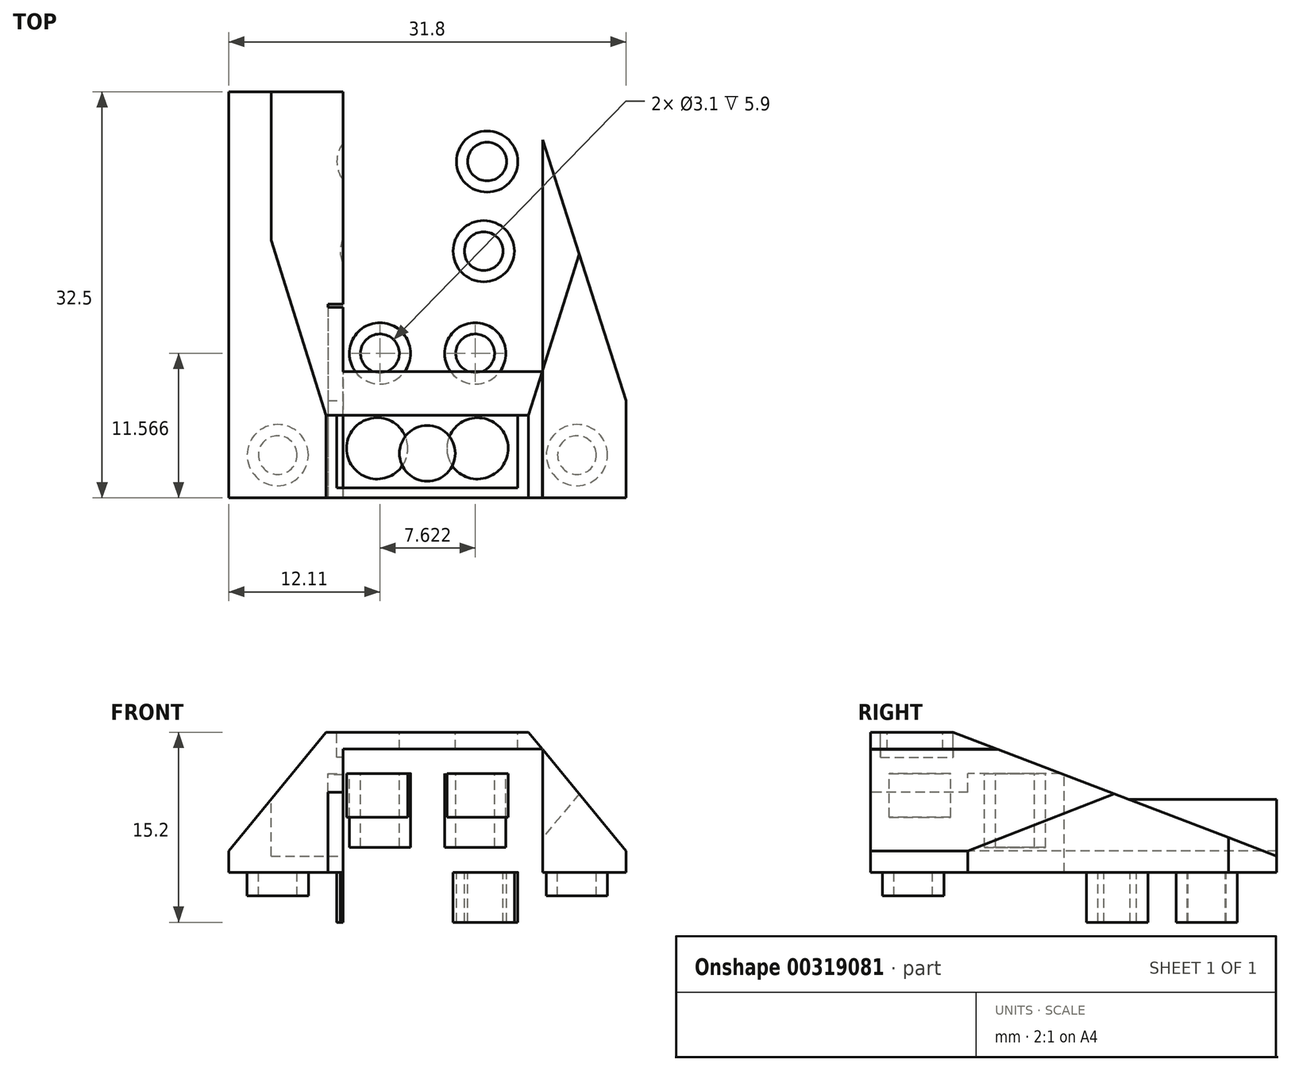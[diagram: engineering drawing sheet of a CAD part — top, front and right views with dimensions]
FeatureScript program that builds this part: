
annotation { "Feature Type Name" : "Feature", "Feature Type Description" : "" }
export const myFeature = defineFeature(function(context is Context, id is Id, definition is map)
    precondition{}
    {
        {
            var Q0;
            Q0=qCreatedBy(makeId("Front.planeOp"),FACE);
            var sketch = newSketch(context, id + "F0", { "sketchPlane" : qUnion([Q0])});
            skLineSegment(sketch, "E0.bottom", {"start": v(-15.9, 3.2) * mm, "end": v(15.9, 3.2) * mm});
            skLineSegment(sketch, "E0.top", {"start": v(-15.9, -6.5) * mm, "end": v(15.9, -6.5) * mm});
            skLineSegment(sketch, "E0.left", {"start": v(-15.9, 3.2) * mm, "end": v(-15.9, -6.5) * mm});
            skLineSegment(sketch, "E0.right", {"start": v(15.9, 3.2) * mm, "end": v(15.9, -6.5) * mm});
            skLineSegment(sketch, "E1.bottom", {"start": v(-6.73, -6.5) * mm, "end": v(9.23, -6.5) * mm});
            skLineSegment(sketch, "E1.top", {"start": v(-6.73, 1.85) * mm, "end": v(9.23, 1.85) * mm});
            skLineSegment(sketch, "E1.left", {"start": v(-6.73, -6.5) * mm, "end": v(-6.73, 1.85) * mm});
            skLineSegment(sketch, "E1.right", {"start": v(9.23, -6.5) * mm, "end": v(9.23, 1.85) * mm});
            skSolve(sketch);
        }
        {
            var Q0;
            Q0=makeQuery(id+"F0.imprint","IMPRINT",FACE,{"disambiguationData":[TD([[makeQuery(id+"F0.imprint","IMPRINT",EDGE,{"derivedFrom":sQuery(id+"F0.wireOp",EDGE,"E0.bottom")}),-1.0]])]});
            var Q1;
            Q1=makeQuery(id+"F0.imprint","IMPRINT",FACE,{"disambiguationData":[TD([[makeQuery(id+"F0.imprint","IMPRINT",EDGE,{"derivedFrom":sQuery(id+"F0.wireOp",EDGE,"E1.bottom")}),1.0]])]});
            extrude(context, id + "F1", {"entities" : qUnion([Q0, Q1]), "depth" : 32.5 * mm});
        }
        {
            var Q0;
            Q0=makeQuery(id+"F1.opExtrude","CAP_FACE",FACE,{"disambiguationData":[OSD([sQuery(id+"F0.wireOp",EDGE,"E0.bottom"),sQuery(id+"F0.wireOp",EDGE,"E0.top"),sQuery(id+"F0.wireOp",EDGE,"E0.left"),sQuery(id+"F0.wireOp",EDGE,"E0.right"),sQuery(id+"F0.wireOp",EDGE,"E1.bottom")])],"isStart":false});
            var sketch = newSketch(context, id + "F2", { "sketchPlane" : qUnion([Q0])});
            skLineSegment(sketch, "E2.bottom", {"start": v(-7.95, -6.5) * mm, "end": v(7.95, -6.5) * mm});
            skLineSegment(sketch, "E2.top", {"start": v(-7.95, -0.1) * mm, "end": v(7.95, -0.1) * mm});
            skLineSegment(sketch, "E2.left", {"start": v(-7.95, -6.5) * mm, "end": v(-7.95, -0.1) * mm});
            skLineSegment(sketch, "E2.right", {"start": v(7.95, -6.5) * mm, "end": v(7.95, -0.1) * mm});
            skLineSegment(sketch, "E3", {"start": v(-15.9, -6.5) * mm, "end": v(-7.95, -6.5) * mm});
            skLineSegment(sketch, "E4", {"start": v(7.95, -6.5) * mm, "end": v(15.9, -6.5) * mm});
            skLineSegment(sketch, "E5", {"start": v(8.1, 3.2) * mm, "end": v(15.9, -6.3) * mm});
            skLineSegment(sketch, "E6", {"start": v(-8.1, 3.2) * mm, "end": v(-15.9, -6.3) * mm});
            skSolve(sketch);
        }
        {
            var Q0;
            Q0=makeQuery(id+"F2.imprint","IMPRINT",FACE,{"disambiguationData":[TD([[makeQuery(id+"F2.imprint","IMPRINT",EDGE,{"derivedFrom":sQuery(id+"F2.wireOp",EDGE,"E2.bottom")}),1.0]])]});
            extrude(context, id + "F3", {"entities" : qUnion([Q0]), "operationType" : NewBodyOperationType.REMOVE, "oppositeDirection" : true, "depth" : 15.5 * mm});
        }
        {
            var Q0;
            {var subQ0=sQuery(id+"F2.wireOp",EDGE,"E6");Q0=makeQuery(id+"F2.imprint","IMPRINT",FACE,{"disambiguationData":[TD([[makeQuery(id+"F2.imprint","IMPRINT",EDGE,{"derivedFrom":subQ0}),-1.0]])]});}
            var Q1;
            {var subQ0=sQuery(id+"F2.wireOp",EDGE,"E5");Q1=makeQuery(id+"F2.imprint","IMPRINT",FACE,{"disambiguationData":[TD([[makeQuery(id+"F2.imprint","IMPRINT",EDGE,{"derivedFrom":subQ0}),1.0]])]});}
            extrude(context, id + "F4", {"entities" : qUnion([Q0, Q1]), "operationType" : NewBodyOperationType.REMOVE, "oppositeDirection" : true, "depth" : 70 * mm});
        }
        {
            var Q0;
            Q0=makeQuery(id+"F1.opExtrude","SWEPT_FACE",FACE,{"disambiguationData":[OSD([sQuery(id+"F0.wireOp",EDGE,"E0.top"),sQuery(id+"F0.wireOp",EDGE,"E1.bottom")])]});
            var sketch = newSketch(context, id + "F5", { "sketchPlane" : qUnion([Q0])});
            skLineSegment(sketch, "E7", {"start": v(-15.9, 24.7) * mm, "end": v(-8, 0) * mm});
            skLineSegment(sketch, "E8", {"start": v(15.9, 24.7) * mm, "end": v(8, 0) * mm});
            skSolve(sketch);
        }
        {
            var Q0;
            {var subQ0=sQuery(id+"F5.wireOp",EDGE,"E7");Q0=makeQuery(id+"F5.imprint","IMPRINT",FACE,{"disambiguationData":[TD([[makeQuery(id+"F5.imprint","IMPRINT",EDGE,{"derivedFrom":subQ0}),-1.0]])]});}
            var Q1;
            {var subQ0=sQuery(id+"F5.wireOp",EDGE,"E8");Q1=makeQuery(id+"F5.imprint","IMPRINT",FACE,{"disambiguationData":[TD([[makeQuery(id+"F5.imprint","IMPRINT",EDGE,{"derivedFrom":subQ0}),1.0]])]});}
            extrude(context, id + "F6", {"entities" : qUnion([Q0, Q1]), "operationType" : NewBodyOperationType.REMOVE, "oppositeDirection" : true, "depth" : 25 * mm});
        }
        {
            var Q0;
            Q0=makeQuery(id+"F3.boolean.opBoolean","COPY",FACE,{"derivedFrom":makeQuery(id+"F3.opExtrude","SWEPT_FACE",FACE,{"disambiguationData":[OSD([sQuery(id+"F2.wireOp",EDGE,"E2.top")])]})});
            var sketch = newSketch(context, id + "F7", { "sketchPlane" : qUnion([Q0])});
            skLineSegment(sketch, "E9", {"start": v(-7.95, 24.7) * mm, "end": v(7.95, 24.7) * mm});
            skCircle(sketch, "E10", {"center": v(-4.01, 28.54) * mm, "radius": 2.45 * mm});
            skCircle(sketch, "E11", {"center": v(4.01, 28.54) * mm, "radius": 2.45 * mm});
            skSolve(sketch);
        }
        {
            var Q0;
            Q0=makeQuery(id+"F7.imprint","IMPRINT",FACE,{"disambiguationData":[TD([[makeQuery(id+"F7.imprint","IMPRINT",EDGE,{"derivedFrom":sQuery(id+"F7.wireOp",EDGE,"E10")}),1.0]])]});
            var Q1;
            Q1=makeQuery(id+"F7.imprint","IMPRINT",FACE,{"disambiguationData":[TD([[makeQuery(id+"F7.imprint","IMPRINT",EDGE,{"derivedFrom":sQuery(id+"F7.wireOp",EDGE,"E11")}),1.0]])]});
            extrude(context, id + "F8", {"entities" : qUnion([Q0, Q1]), "operationType" : NewBodyOperationType.ADD, "depth" : 2 * mm});
        }
        {
            var Q0;
            {var subQ2=sQuery(id+"F7.wireOp",EDGE,"E9");Q0=makeQuery(id+"F7.imprint","IMPRINT",FACE,{"disambiguationData":[TD([[makeQuery(id+"F7.imprint","IMPRINT",EDGE,{"derivedFrom":subQ2}),1.0]])]});}
            var Q1;
            Q1=makeQuery(id+"F1.opExtrude","SWEPT_FACE",FACE,{"disambiguationData":[OSD([sQuery(id+"F0.wireOp",EDGE,"E0.top"),sQuery(id+"F0.wireOp",EDGE,"E1.bottom")])]});
            var Q2;
            Q2=makeQuery(id+"F8.opExtrude","CAP_FACE",FACE,{"disambiguationData":[OSD([sQuery(id+"F7.wireOp",EDGE,"E10")])],"isStart":false});
            var Q3;
            Q3=makeQuery(id+"F8.opExtrude","CAP_FACE",FACE,{"disambiguationData":[OSD([sQuery(id+"F7.wireOp",EDGE,"E11")])],"isStart":false});
            extrude(context, id + "F9", {"entities" : qUnion([Q0, Q1, Q2, Q3]), "operationType" : NewBodyOperationType.ADD, "depth" : 1.5 * mm});
        }
        {
            var Q0;
            {var subQ0=sQuery(id+"F7.wireOp",EDGE,"E9");Q0=makeQuery(id+"F7.imprint","IMPRINT",FACE,{"disambiguationData":[TD([[makeQuery(id+"F7.imprint","IMPRINT",EDGE,{"derivedFrom":subQ0}),-1.0]])]});}
            var sketch = newSketch(context, id + "F10", { "sketchPlane" : qUnion([Q0])});
            skCircle(sketch, "E12", {"center": v(-3.79, 20.93) * mm, "radius": 2.45 * mm});
            skCircle(sketch, "E13", {"center": v(3.83, 20.93) * mm, "radius": 2.45 * mm});
            skCircle(sketch, "E14", {"center": v(-3.79, 20.93) * mm, "radius": 1.55 * mm});
            skCircle(sketch, "E15", {"center": v(3.83, 20.93) * mm, "radius": 1.55 * mm});
            skSolve(sketch);
        }
        {
            var Q0;
            Q0 = qSketchRegion(id + "F10", true);
            extrude(context, id + "F11", {"entities" : qUnion([Q0]), "operationType" : NewBodyOperationType.ADD, "depth" : 5.9 * mm});
        }
        {
            var Q0;
            Q0=makeQuery(id+"F9.opExtrude","CAP_FACE",FACE,{"disambiguationData":[OSD([sQuery(id+"F0.wireOp",EDGE,"E0.top"),sQuery(id+"F0.wireOp",EDGE,"E1.bottom")])],"isStart":false});
            var sketch = newSketch(context, id + "F12", { "sketchPlane" : qUnion([Q0])});
            skCircle(sketch, "E16", {"center": v(-11.97, 29.07) * mm, "radius": 2.45 * mm});
            skCircle(sketch, "E17", {"center": v(11.97, 29.07) * mm, "radius": 2.45 * mm});
            skCircle(sketch, "E18", {"center": v(-11.97, 29.07) * mm, "radius": 1.55 * mm});
            skCircle(sketch, "E19", {"center": v(11.97, 29.07) * mm, "radius": 1.55 * mm});
            skCircle(sketch, "E20", {"center": v(-4.51, 12.76) * mm, "radius": 2.45 * mm});
            skCircle(sketch, "E21", {"center": v(4.51, 12.76) * mm, "radius": 2.45 * mm});
            skCircle(sketch, "E22", {"center": v(-4.78, 5.59) * mm, "radius": 2.45 * mm});
            skCircle(sketch, "E23", {"center": v(4.78, 5.59) * mm, "radius": 2.45 * mm});
            skCircle(sketch, "E24", {"center": v(-4.51, 12.76) * mm, "radius": 1.55 * mm});
            skCircle(sketch, "E25", {"center": v(-4.78, 5.59) * mm, "radius": 1.55 * mm});
            skCircle(sketch, "E26", {"center": v(4.51, 12.76) * mm, "radius": 1.55 * mm});
            skCircle(sketch, "E27", {"center": v(4.78, 5.59) * mm, "radius": 1.55 * mm});
            skSolve(sketch);
        }
        {
            var Q0;
            Q0=makeQuery(id+"F12.imprint","IMPRINT",FACE,{"disambiguationData":[TD([[makeQuery(id+"F12.imprint","IMPRINT",EDGE,{"derivedFrom":sQuery(id+"F12.wireOp",EDGE,"E16")}),1.0]])]});
            var Q1;
            Q1=makeQuery(id+"F12.imprint","IMPRINT",FACE,{"disambiguationData":[TD([[makeQuery(id+"F12.imprint","IMPRINT",EDGE,{"derivedFrom":sQuery(id+"F12.wireOp",EDGE,"E17")}),1.0]])]});
            extrude(context, id + "F13", {"entities" : qUnion([Q0, Q1]), "operationType" : NewBodyOperationType.ADD, "depth" : 1.9 * mm});
        }
        {
            var Q0;
            Q0=makeQuery(id+"F12.imprint","IMPRINT",FACE,{"disambiguationData":[TD([[makeQuery(id+"F12.imprint","IMPRINT",EDGE,{"derivedFrom":sQuery(id+"F12.wireOp",EDGE,"E20")}),1.0]])]});
            var Q1;
            Q1=makeQuery(id+"F12.imprint","IMPRINT",FACE,{"disambiguationData":[TD([[makeQuery(id+"F12.imprint","IMPRINT",EDGE,{"derivedFrom":sQuery(id+"F12.wireOp",EDGE,"E21")}),1.0]])]});
            extrude(context, id + "F14", {"entities" : qUnion([Q0, Q1]), "operationType" : NewBodyOperationType.ADD, "depth" : 4 * mm});
        }
        {
            var Q0;
            Q0=makeQuery(id+"F12.imprint","IMPRINT",FACE,{"disambiguationData":[TD([[makeQuery(id+"F12.imprint","IMPRINT",EDGE,{"derivedFrom":sQuery(id+"F12.wireOp",EDGE,"E22")}),1.0]])]});
            var Q1;
            Q1=makeQuery(id+"F12.imprint","IMPRINT",FACE,{"disambiguationData":[TD([[makeQuery(id+"F12.imprint","IMPRINT",EDGE,{"derivedFrom":sQuery(id+"F12.wireOp",EDGE,"E23")}),1.0]])]});
            extrude(context, id + "F15", {"entities" : qUnion([Q0, Q1]), "operationType" : NewBodyOperationType.ADD, "depth" : 4 * mm});
        }
        {
            var Q0;
            Q0=makeQuery(id+"F1.opExtrude","SWEPT_FACE",FACE,{"disambiguationData":[OSD([sQuery(id+"F0.wireOp",EDGE,"E0.bottom")])]});
            var sketch = newSketch(context, id + "F16", { "sketchPlane" : qUnion([Q0])});
            skLineSegment(sketch, "E28", {"start": v(8.1, -24.72) * mm, "end": v(-8.1, -24.72) * mm});
            skCircle(sketch, "E29", {"center": v(0, -28.94) * mm, "radius": 2.23 * mm});
            skLineSegment(sketch, "E30.bottom", {"start": v(7.22, -31.7) * mm, "end": v(-7.25, -31.7) * mm});
            skLineSegment(sketch, "E30.top", {"start": v(7.22, -25.9) * mm, "end": v(-7.25, -25.9) * mm});
            skLineSegment(sketch, "E30.left", {"start": v(7.22, -31.7) * mm, "end": v(7.22, -25.9) * mm});
            skLineSegment(sketch, "E30.right", {"start": v(-7.25, -31.7) * mm, "end": v(-7.25, -25.9) * mm});
            skSolve(sketch);
        }
        {
            var Q0;
            Q0=makeQuery(id+"F16.imprint","IMPRINT",FACE,{"disambiguationData":[TD([[makeQuery(id+"F16.imprint","IMPRINT",EDGE,{"derivedFrom":sQuery(id+"F16.wireOp",EDGE,"E29")}),-1.0]])]});
            extrude(context, id + "F17", {"entities" : qUnion([Q0]), "operationType" : NewBodyOperationType.REMOVE, "oppositeDirection" : true, "depth" : 2 * mm});
        }
        {
            var Q0;
            Q0=qCreatedBy(makeId("Right.planeOp"),FACE);
            var sketch = newSketch(context, id + "F18", { "sketchPlane" : qUnion([Q0])});
            skLineSegment(sketch, "E31", {"start": v(0, -6.7) * mm, "end": v(-25.89, 3.2) * mm});
            skLineSegment(sketch, "E32", {"start": v(-0.31, 3.2) * mm, "end": v(0, 3.2) * mm});
            skLineSegment(sketch, "E33", {"start": v(0, -6.7) * mm, "end": v(0, 3.2) * mm});
            skLineSegment(sketch, "E34", {"start": v(-25.89, 3.2) * mm, "end": v(0, 3.2) * mm});
            skSolve(sketch);
        }
        {
            var Q0;
            {var subQ0=sQuery(id+"F18.wireOp",EDGE,"E34");var subQ1=sQuery(id+"F18.wireOp",EDGE,"E31");var subQ2=makeQuery(id+"F18.imprint","INTERSECT",VERTEX,{"derivedFrom":[subQ1,subQ0]});Q0=makeQuery(id+"F18.imprint","IMPRINT",FACE,{"disambiguationData":[TD([[makeQuery(id+"F18.imprint","IMPRINT",EDGE,{"disambiguationData":[TD([[subQ2,1.0]])],"derivedFrom":subQ1}),1.0]])]});}
            var Q1;
            {var subQ0=sQuery(id+"F18.wireOp",EDGE,"E33");Q1=makeQuery(id+"F18.imprint","IMPRINT",FACE,{"disambiguationData":[TD([[makeQuery(id+"F18.imprint","IMPRINT",EDGE,{"derivedFrom":subQ0}),1.0]])]});}
            extrude(context, id + "F19", {"entities" : qUnion([Q0, Q1]), "operationType" : NewBodyOperationType.REMOVE, "endBound" : BoundingType.SYMMETRIC, "oppositeDirection" : true, "depth" : 25 * mm});
        }
    });
